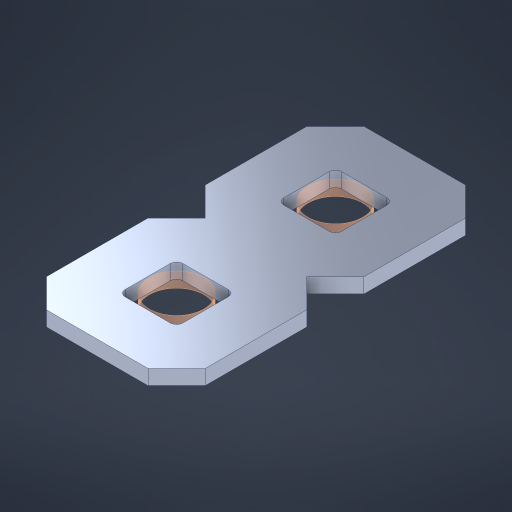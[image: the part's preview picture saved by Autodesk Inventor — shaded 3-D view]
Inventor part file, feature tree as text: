
AUTODESK INVENTOR PART (.ipt)
format: ipt  version: 2023 (Build 270158000, 158)  size: 285,696 bytes
history: native  units: in
note: dims shown in document units (in); Inventor stores cm internally (conversion verified against a paired STEP export)
features: other x3, sketch x2, pattern_linear x1, extrude x1
ambient origin geometry x8: Origin, YZ Plane, XZ Plane, XY Plane, X Axis, Y Axis, Z Axis, Center Point
bodies: Solid1 (feature_tree), Body (feature_tree)
feature tree (7):
  pattern_linear  "Rectangular Pattern1"  Spacing1=0.09in  [1 undecoded]
  sketch  "Sketch1"  dims[d1=0.5in]
  sketch  "Sketch2"  dims[d2=0.182in d3=0.09in d4=0.09in d5=0.09in d6=0.09in d7=0.09in d8=0.09in d9=0.09in d10=0.09in d11=0.02in d13=0.0in d14=0.172in d15=0.0625in d16=0.0in d19=0.5in d22=0.5in]
  other  "Srf1"
  other  "Srf126"
  other  "Circle"
  extrude  "ExtrusionSrf126"  Depth=0.09in
note: 1 required parameter value undecoded (feature->parameter linkage not recoverable at this tier; creation-order binding heuristic only, values carry confidence <= 0.55)
